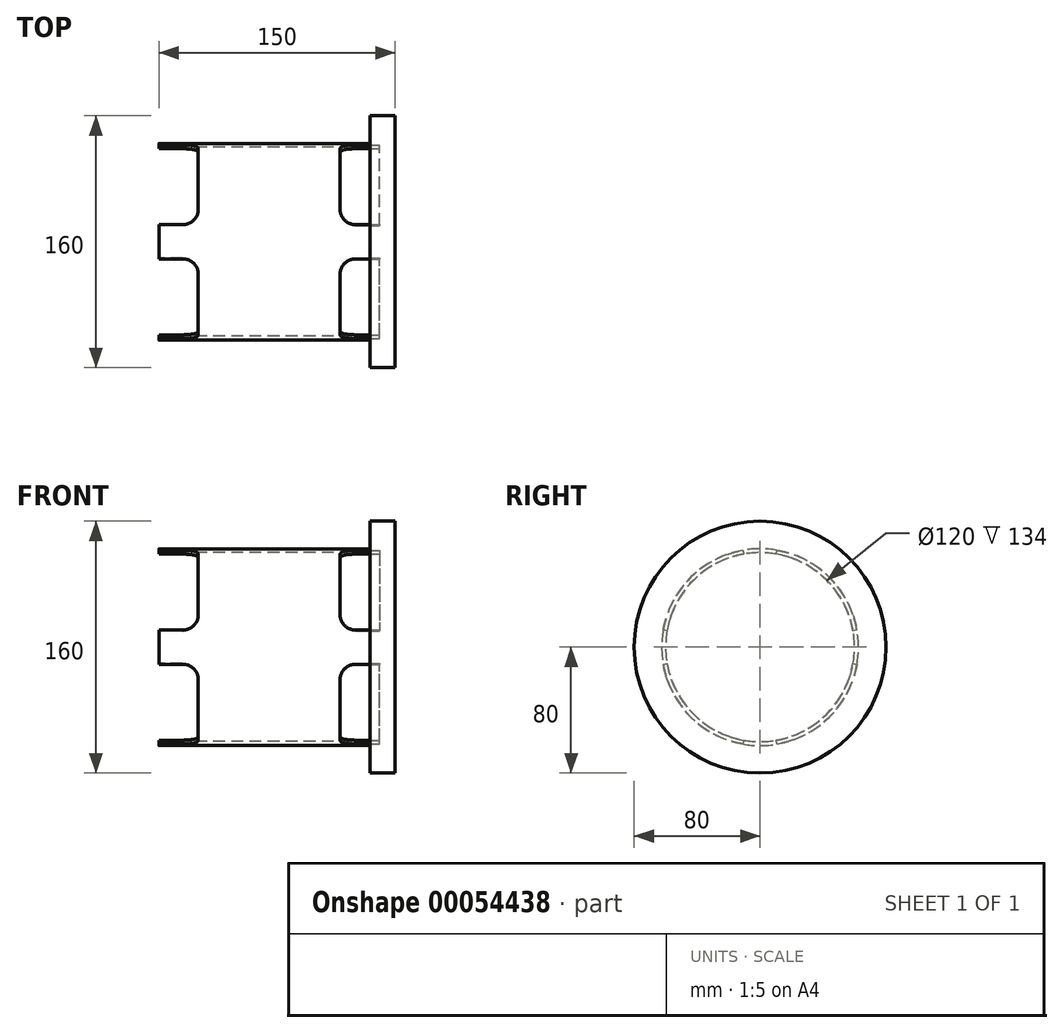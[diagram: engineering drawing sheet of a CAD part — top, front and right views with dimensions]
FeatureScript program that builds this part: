
annotation { "Feature Type Name" : "Feature", "Feature Type Description" : "" }
export const myFeature = defineFeature(function(context is Context, id is Id, definition is map)
    precondition{}
    {
        {
            var Q0;
            Q0=qCreatedBy(makeId("Right.planeOp"),FACE);
            var sketch = newSketch(context, id + "F0", { "sketchPlane" : qUnion([Q0])});
            skCircle(sketch, "E0", {"center": v(0, 0) * mm, "radius": 60 * mm});
            skCircle(sketch, "E1", {"center": v(0, 0) * mm, "radius": 62.5 * mm});
            skSolve(sketch);
        }
        {
            var Q0;
            Q0=makeQuery(id+"F0.imprint","IMPRINT",FACE,{"disambiguationData":[TD([[makeQuery(id+"F0.imprint","IMPRINT",EDGE,{"derivedFrom":sQuery(id+"F0.wireOp",EDGE,"E0")}),-1.0]])]});
            extrude(context, id + "F1", {"entities" : qUnion([Q0]), "depth" : 70 * mm});
        }
        {
            var Q0;
            Q0=makeQuery(id+"F1.opExtrude","CAP_FACE",FACE,{"disambiguationData":[OSD([sQuery(id+"F0.wireOp",EDGE,"E0"),sQuery(id+"F0.wireOp",EDGE,"E1")])],"isStart":false});
            var sketch = newSketch(context, id + "F2", { "sketchPlane" : qUnion([Q0])});
            skCircle(sketch, "E2", {"center": v(0, 0) * mm, "radius": 80 * mm});
            skSolve(sketch);
        }
        {
            var Q0;
            Q0=makeQuery(id+"F2.imprint","IMPRINT",FACE,{"disambiguationData":[TD([[makeQuery(id+"F2.imprint","IMPRINT",EDGE,{"derivedFrom":sQuery(id+"F2.wireOp",EDGE,"E2")}),1.0]])]});
            var Q1;
            Q1=makeQuery(id+"F2.imprint","IMPRINT",FACE,{"disambiguationData":[TD([[makeQuery(id+"F2.imprint","IMPRINT",EDGE,{"derivedFrom":makeQuery(id+"F1.opExtrude","CAP_EDGE",EDGE,{"disambiguationData":[OSD([sQuery(id+"F0.wireOp",EDGE,"E0")])],"isStart":false})}),1.0]])]});
            var Q2;
            Q2=makeQuery(id+"F2.imprint","IMPRINT",FACE,{"disambiguationData":[TD([[makeQuery(id+"F2.imprint","IMPRINT",EDGE,{"derivedFrom":makeQuery(id+"F1.opExtrude","CAP_EDGE",EDGE,{"disambiguationData":[OSD([sQuery(id+"F0.wireOp",EDGE,"E0")])],"isStart":false})}),-1.0]])]});
            extrude(context, id + "F3", {"entities" : qUnion([Q0, Q1, Q2]), "oppositeDirection" : true, "depth" : 6 * mm});
        }
        {
            var Q0;
            Q0=makeQuery(id+"F2.imprint","IMPRINT",FACE,{"disambiguationData":[TD([[makeQuery(id+"F2.imprint","IMPRINT",EDGE,{"derivedFrom":sQuery(id+"F2.wireOp",EDGE,"E2")}),1.0]])]});
            var Q1;
            Q1=makeQuery(id+"F2.imprint","IMPRINT",FACE,{"disambiguationData":[TD([[makeQuery(id+"F2.imprint","IMPRINT",EDGE,{"derivedFrom":makeQuery(id+"F1.opExtrude","CAP_EDGE",EDGE,{"disambiguationData":[OSD([sQuery(id+"F0.wireOp",EDGE,"E0")])],"isStart":false})}),-1.0]])]});
            var Q2;
            Q2=makeQuery(id+"F2.imprint","IMPRINT",FACE,{"disambiguationData":[TD([[makeQuery(id+"F2.imprint","IMPRINT",EDGE,{"derivedFrom":makeQuery(id+"F1.opExtrude","CAP_EDGE",EDGE,{"disambiguationData":[OSD([sQuery(id+"F0.wireOp",EDGE,"E0")])],"isStart":false})}),1.0]])]});
            extrude(context, id + "F4", {"entities" : qUnion([Q0, Q1, Q2]), "depth" : 10 * mm});
        }
        {
            var Q0;
            Q0=makeQuery(id+"F1.opExtrude","CAP_FACE",FACE,{"disambiguationData":[OSD([sQuery(id+"F0.wireOp",EDGE,"E0"),sQuery(id+"F0.wireOp",EDGE,"E1")])],"isStart":false});
            var sketch = newSketch(context, id + "F5", { "sketchPlane" : qUnion([Q0])});
            skLineSegment(sketch, "E3", {"start": v(0, 0) * mm, "end": v(-17.04, -96.64) * mm});
            skLineSegment(sketch, "E4", {"start": v(-17.04, -96.64) * mm, "end": v(-98.48, -17.36) * mm});
            skLineSegment(sketch, "E5", {"start": v(-98.48, -17.36) * mm, "end": v(0, 0) * mm});
            skLineSegment(sketch, "E6.1.0", {"start": v(0, 0) * mm, "end": v(96.64, -17.04) * mm});
            skLineSegment(sketch, "E6.1.1", {"start": v(96.64, -17.04) * mm, "end": v(17.36, -98.48) * mm});
            skLineSegment(sketch, "E6.1.2", {"start": v(17.36, -98.48) * mm, "end": v(0, 0) * mm});
            skLineSegment(sketch, "E6.2.0", {"start": v(0, 0) * mm, "end": v(17.04, 96.64) * mm});
            skLineSegment(sketch, "E6.2.1", {"start": v(17.04, 96.64) * mm, "end": v(98.48, 17.36) * mm});
            skLineSegment(sketch, "E6.2.2", {"start": v(98.48, 17.36) * mm, "end": v(0, 0) * mm});
            skLineSegment(sketch, "E6.3.0", {"start": v(0, 0) * mm, "end": v(-96.64, 17.04) * mm});
            skLineSegment(sketch, "E6.3.1", {"start": v(-96.64, 17.04) * mm, "end": v(-17.36, 98.48) * mm});
            skLineSegment(sketch, "E6.3.2", {"start": v(-17.36, 98.48) * mm, "end": v(0, 0) * mm});
            skPoint(sketch, "E6.center", {"position": v(0, 0) * mm});
            skSolve(sketch);
        }
        {
            var Q0;
            {var subQ0=sQuery(id+"F5.wireOp",EDGE,"E6.1.0");var subQ1=makeQuery(id+"F1.opExtrude","CAP_EDGE",EDGE,{"disambiguationData":[OSD([sQuery(id+"F0.wireOp",EDGE,"E1")])],"isStart":false});var subQ2=makeQuery(id+"F5.imprint","INTERSECT",VERTEX,{"derivedFrom":[subQ1,subQ0]});Q0=makeQuery(id+"F5.imprint","IMPRINT",FACE,{"disambiguationData":[TD([[makeQuery(id+"F5.imprint","IMPRINT",EDGE,{"disambiguationData":[TD([[subQ2,1.0]])],"derivedFrom":subQ0}),-1.0]])]});}
            var Q1;
            {var subQ0=sQuery(id+"F5.wireOp",EDGE,"E3");var subQ1=makeQuery(id+"F1.opExtrude","CAP_EDGE",EDGE,{"disambiguationData":[OSD([sQuery(id+"F0.wireOp",EDGE,"E1")])],"isStart":false});var subQ2=makeQuery(id+"F5.imprint","INTERSECT",VERTEX,{"derivedFrom":[subQ1,subQ0]});Q1=makeQuery(id+"F5.imprint","IMPRINT",FACE,{"disambiguationData":[TD([[makeQuery(id+"F5.imprint","IMPRINT",EDGE,{"disambiguationData":[TD([[subQ2,1.0]])],"derivedFrom":subQ0}),-1.0]])]});}
            var Q2;
            {var subQ0=sQuery(id+"F5.wireOp",EDGE,"E6.3.0");var subQ1=makeQuery(id+"F1.opExtrude","CAP_EDGE",EDGE,{"disambiguationData":[OSD([sQuery(id+"F0.wireOp",EDGE,"E1")])],"isStart":false});var subQ2=makeQuery(id+"F5.imprint","INTERSECT",VERTEX,{"derivedFrom":[subQ1,subQ0]});Q2=makeQuery(id+"F5.imprint","IMPRINT",FACE,{"disambiguationData":[TD([[makeQuery(id+"F5.imprint","IMPRINT",EDGE,{"disambiguationData":[TD([[subQ2,1.0]])],"derivedFrom":subQ0}),-1.0]])]});}
            var Q3;
            {var subQ0=sQuery(id+"F5.wireOp",EDGE,"E6.2.0");var subQ1=makeQuery(id+"F1.opExtrude","CAP_EDGE",EDGE,{"disambiguationData":[OSD([sQuery(id+"F0.wireOp",EDGE,"E1")])],"isStart":false});var subQ2=makeQuery(id+"F5.imprint","INTERSECT",VERTEX,{"derivedFrom":[subQ1,subQ0]});Q3=makeQuery(id+"F5.imprint","IMPRINT",FACE,{"disambiguationData":[TD([[makeQuery(id+"F5.imprint","IMPRINT",EDGE,{"disambiguationData":[TD([[subQ2,1.0]])],"derivedFrom":subQ0}),-1.0]])]});}
            extrude(context, id + "F6", {"entities" : qUnion([Q0, Q1, Q2, Q3]), "operationType" : NewBodyOperationType.REMOVE, "oppositeDirection" : true, "depth" : 25 * mm});
        }
        {
            var Q0;
            Q0=makeQuery(id+"F6.boolean.opBoolean","COPY",EDGE,{"derivedFrom":makeQuery(id+"F6.opExtrude","CAP_EDGE",EDGE,{"disambiguationData":[OSD([sQuery(id+"F5.wireOp",EDGE,"E6.1.0")])],"isStart":false})});
            var Q1;
            Q1=makeQuery(id+"F6.boolean.opBoolean","COPY",EDGE,{"derivedFrom":makeQuery(id+"F6.opExtrude","CAP_EDGE",EDGE,{"disambiguationData":[OSD([sQuery(id+"F5.wireOp",EDGE,"E6.1.2")])],"isStart":false})});
            var Q2;
            Q2=makeQuery(id+"F6.boolean.opBoolean","COPY",EDGE,{"derivedFrom":makeQuery(id+"F6.opExtrude","CAP_EDGE",EDGE,{"disambiguationData":[OSD([sQuery(id+"F5.wireOp",EDGE,"E5")])],"isStart":false})});
            var Q3;
            Q3=makeQuery(id+"F6.boolean.opBoolean","COPY",EDGE,{"derivedFrom":makeQuery(id+"F6.opExtrude","CAP_EDGE",EDGE,{"disambiguationData":[OSD([sQuery(id+"F5.wireOp",EDGE,"E6.2.0")])],"isStart":false})});
            var Q4;
            Q4=makeQuery(id+"F6.boolean.opBoolean","COPY",EDGE,{"derivedFrom":makeQuery(id+"F6.opExtrude","CAP_EDGE",EDGE,{"disambiguationData":[OSD([sQuery(id+"F5.wireOp",EDGE,"E6.2.2")])],"isStart":false})});
            var Q5;
            Q5=makeQuery(id+"F6.boolean.opBoolean","COPY",EDGE,{"derivedFrom":makeQuery(id+"F6.opExtrude","CAP_EDGE",EDGE,{"disambiguationData":[OSD([sQuery(id+"F5.wireOp",EDGE,"E6.3.0")])],"isStart":false})});
            var Q6;
            Q6=makeQuery(id+"F6.boolean.opBoolean","COPY",EDGE,{"derivedFrom":makeQuery(id+"F6.opExtrude","CAP_EDGE",EDGE,{"disambiguationData":[OSD([sQuery(id+"F5.wireOp",EDGE,"E6.3.2")])],"isStart":false})});
            var Q7;
            Q7=makeQuery(id+"F6.boolean.opBoolean","COPY",EDGE,{"derivedFrom":makeQuery(id+"F6.opExtrude","CAP_EDGE",EDGE,{"disambiguationData":[OSD([sQuery(id+"F5.wireOp",EDGE,"E3")])],"isStart":false})});
            fillet(context, id + "F7", {"entities" : qUnion([Q0, Q1, Q2, Q3, Q4, Q5, Q6, Q7]), "radius" : 10 * mm, "tangentPropagation" : true, "allowEdgeOverflow" : false});
        }
        {
            var Q0;
            Q0=makeQuery(id+"F1.opExtrude","SWEPT_BODY",BODY,{"disambiguationData":[OSD([sQuery(id+"F0.wireOp",EDGE,"E0"),sQuery(id+"F0.wireOp",EDGE,"E1")])]});
            var Q1;
            Q1=qCreatedBy(makeId("Right.planeOp"),FACE);
            mirror(context, id + "F8", {"operationType" : NewBodyOperationType.ADD, "entities" : qUnion([Q0]), "mirrorPlane" : qUnion([Q1])});
        }
    });
